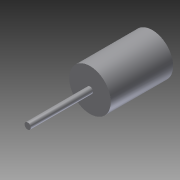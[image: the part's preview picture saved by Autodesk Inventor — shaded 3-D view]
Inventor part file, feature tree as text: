
AUTODESK INVENTOR PART (.ipt)
format: ipt  version: 2012 (Build 160160000, 160)  size: 85,504 bytes
history: native  units: in
note: dims shown in document units (in); Inventor stores cm internally (conversion verified against a paired STEP export)
features: extrude x2, sketch x2
ambient origin geometry x8: Origin, YZ Plane, XZ Plane, XY Plane, X Axis, Y Axis, Z Axis, Center Point
bodies: Solid1 (feature_tree)
feature tree (4):
  extrude  "Extrusion1"  Depth=3.0in TaperAngle=0.0deg
  extrude  "Extrusion2"  Depth=3.0in TaperAngle=0.0deg
  sketch  "Sketch1"  dims[d0=2.0in d1=3.0in d2=0.0in]
  sketch  "Sketch2"  dims[d3=0.3in d4=3.0in d5=0.0in]
